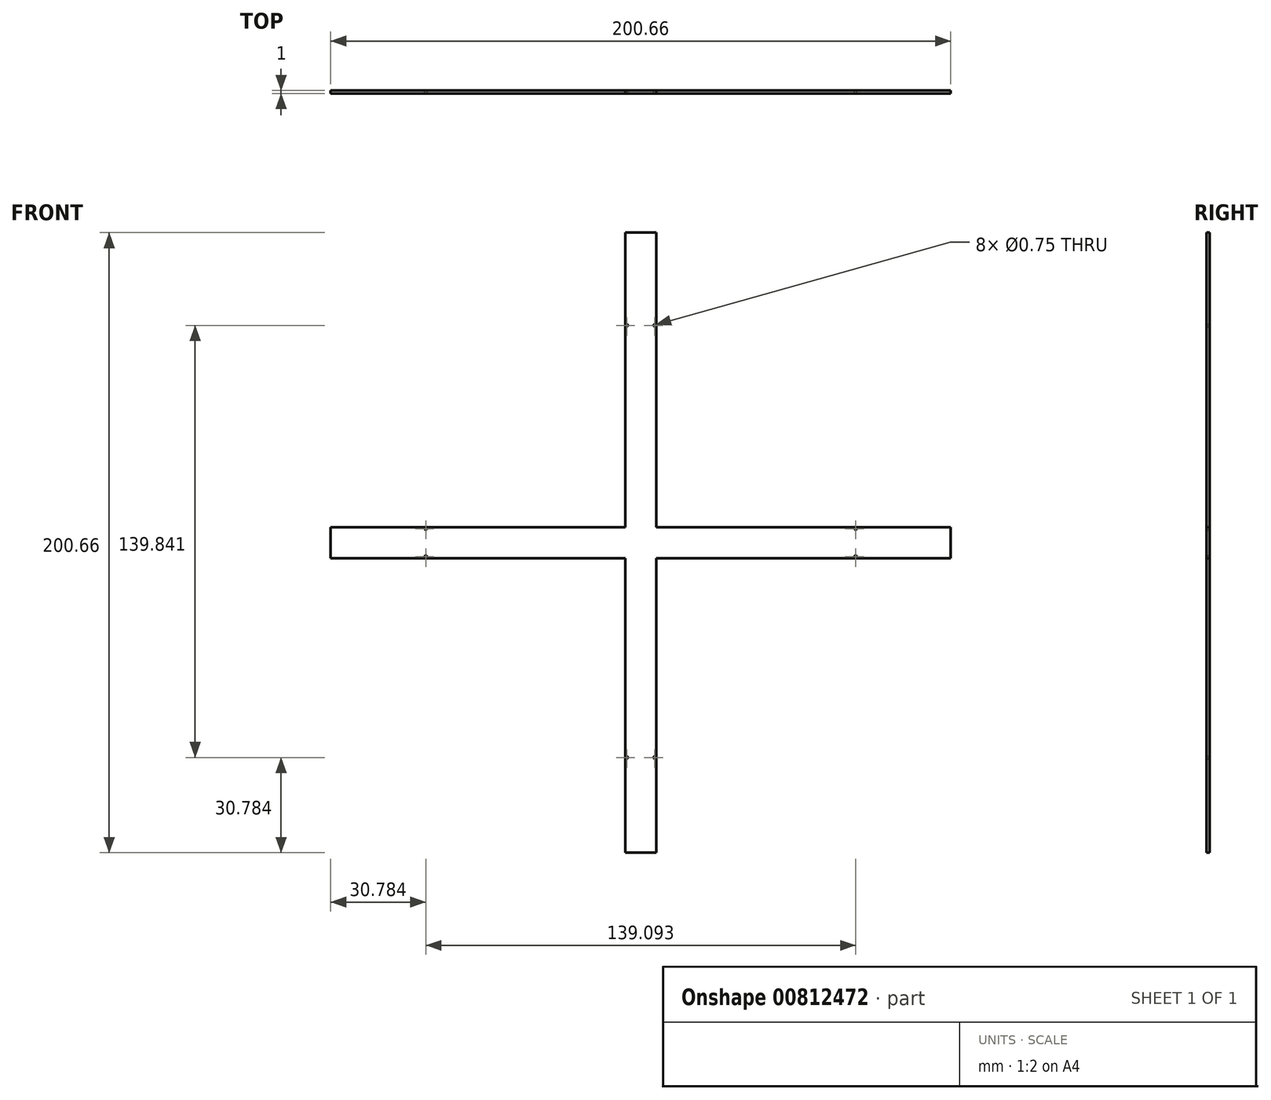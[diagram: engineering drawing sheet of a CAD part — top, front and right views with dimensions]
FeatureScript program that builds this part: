
annotation { "Feature Type Name" : "Feature", "Feature Type Description" : "" }
export const myFeature = defineFeature(function(context is Context, id is Id, definition is map)
    precondition{}
    {
        {
            var Q0;
            Q0=qCreatedBy(makeId("Front.planeOp"),FACE);
            var sketch = newSketch(context, id + "F0", { "sketchPlane" : qUnion([Q0])});
            skLineSegment(sketch, "E0.top", {"start": v(-5, -100.33) * mm, "end": v(5, -100.33) * mm});
            skLineSegment(sketch, "E0.left", {"start": v(-100.33, 5) * mm, "end": v(-100.33, -5) * mm});
            skLineSegment(sketch, "E0.right", {"start": v(100.33, 5) * mm, "end": v(100.33, -5) * mm});
            skLineSegment(sketch, "E1", {"start": v(-100.33, 5) * mm, "end": v(-5, 5) * mm});
            skLineSegment(sketch, "E2", {"start": v(-100.33, -5) * mm, "end": v(-5, -5) * mm});
            skLineSegment(sketch, "E3.trimOffspring", {"start": v(-5, -5) * mm, "end": v(-5, -100.33) * mm});
            skLineSegment(sketch, "E4.trimOffspring", {"start": v(5, 5) * mm, "end": v(100.33, 5) * mm});
            skLineSegment(sketch, "E5.trimOffspring", {"start": v(5, -5) * mm, "end": v(5, -100.33) * mm});
            skLineSegment(sketch, "E6.trimOffspring", {"start": v(5, -5) * mm, "end": v(100.33, -5) * mm});
            skLineSegment(sketch, "E7", {"start": v(-5, 5) * mm, "end": v(-5, 100.33) * mm});
            skLineSegment(sketch, "E8", {"start": v(5, 5) * mm, "end": v(5, 100.33) * mm});
            skLineSegment(sketch, "E9", {"start": v(-5, 100.33) * mm, "end": v(5, 100.33) * mm});
            skCircle(sketch, "E10", {"center": v(-69.55, 4.51) * mm, "radius": 0.37 * mm});
            skCircle(sketch, "E11", {"center": v(-69.55, -4.51) * mm, "radius": 0.37 * mm});
            skCircle(sketch, "E12", {"center": v(4.51, -69.55) * mm, "radius": 0.37 * mm});
            skCircle(sketch, "E13", {"center": v(-4.51, -69.55) * mm, "radius": 0.37 * mm});
            skCircle(sketch, "E14", {"center": v(-4.51, 70.3) * mm, "radius": 0.37 * mm});
            skCircle(sketch, "E15", {"center": v(4.51, 70.3) * mm, "radius": 0.37 * mm});
            skCircle(sketch, "E16", {"center": v(69.55, 4.51) * mm, "radius": 0.37 * mm});
            skCircle(sketch, "E17", {"center": v(69.55, -4.51) * mm, "radius": 0.37 * mm});
            skSolve(sketch);
        }
        {
            var Q0;
            Q0=makeQuery(id+"F0.imprint","IMPRINT",FACE,{"disambiguationData":[TD([[makeQuery(id+"F0.imprint","IMPRINT",EDGE,{"derivedFrom":sQuery(id+"F0.wireOp",EDGE,"E0.top")}),1.0]])]});
            extrude(context, id + "F1", {"entities" : qUnion([Q0]), "depth" : 1 * mm, "offsetDistance" : 25 * mm});
        }
    });
